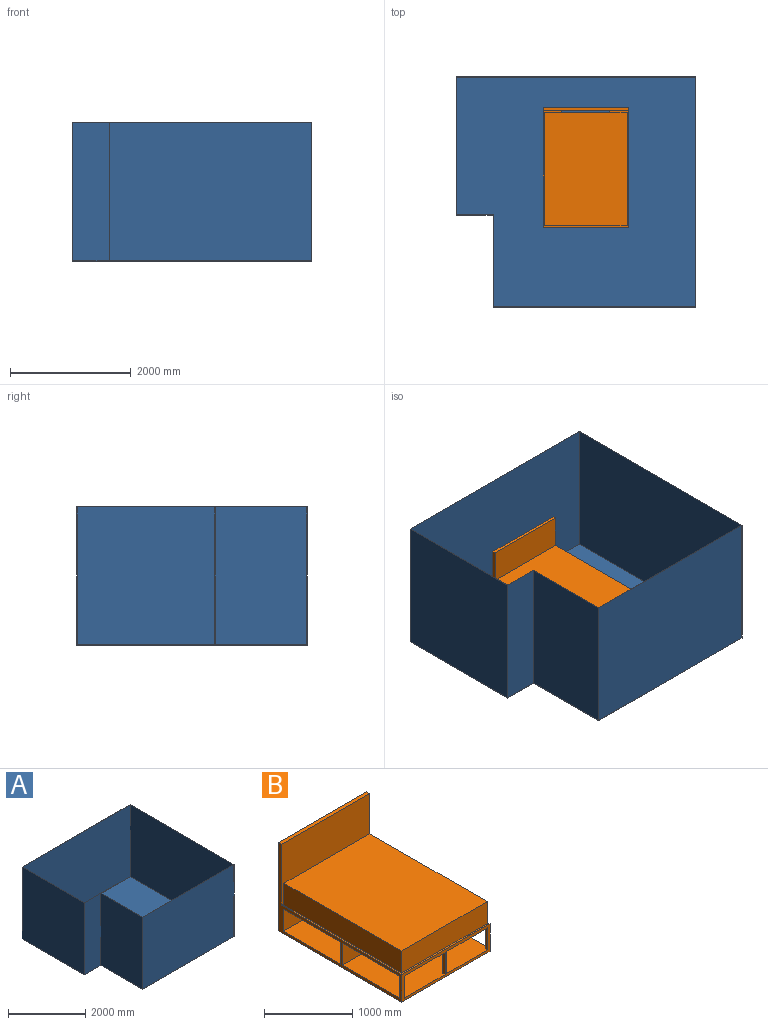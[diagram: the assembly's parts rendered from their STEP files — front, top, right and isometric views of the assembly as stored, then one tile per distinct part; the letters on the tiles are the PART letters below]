
ASSEMBLY  parts=2 mates=2
PART A: 15 faces, bbox 3962.4x3810x2286 mm
  f0: plane 3962.4x3810mm, normal (0,0,1), area 39458mm2, adj f1,f2,f3,f4,f5,f6,f8,f9
  f1: plane 3810x2286mm, normal (1,0,0), area 8709660mm2, adj f0,f2,f6,f7
  f2: plane 3962.4x2286mm, normal (0,1,0), area 9058046.4mm2, adj f0,f1,f3,f7
  f3: plane 2286x2286mm, normal (-1,0,0), area 5225796mm2, adj f0,f2,f4,f7
  f4: plane 2286x609.6mm, normal (0,-1,0), area 1393545.6mm2, adj f0,f3,f5,f7
  f5: plane 2286x1524mm, normal (-1,0,0), area 3483864mm2, adj f0,f4,f6,f7
  f6: plane 3352.8x2286mm, normal (0,-1,0), area 7664500.8mm2, adj f0,f1,f5,f7
  f7: plane 3962.4x3810mm, normal (0,0,-1), area 14167713.6mm2, adj f1,f2,f3,f4,f5,f6
  f8: plane 3804.92x2283.46mm, normal (-1,0,0), area 8688382.6mm2, adj f0,f9,f13,f14
  f9: plane 3957.32x2283.46mm, normal (0,-1,0), area 9036381.9mm2, adj f0,f8,f10,f14
  f10: plane 2283.46x2280.92mm, normal (1,0,0), area 5208389.6mm2, adj f0,f9,f11,f14
  f11: plane 2283.46x609.6mm, normal (0,1,0), area 1391997.2mm2, adj f0,f10,f12,f14
  f12: plane 2283.46x1524mm, normal (1,0,0), area 3479993mm2, adj f0,f11,f13,f14
  f13: plane 3347.72x2283.46mm, normal (0,1,0), area 7644384.7mm2, adj f0,f8,f12,f14
  f14: plane 3957.32x3804.92mm, normal (0,0,1), area 14128255.6mm2, adj f8,f9,f10,f11,f12,f13
PART B: 37 faces, bbox 1409.7x1981.2x1219.2 mm
  f0: plane 304.8x25.4mm, normal (0,1,0), area 7741.9mm2, adj f23,f24,f33,f36
  f1: plane 304.8x38.1mm, normal (0,1,0), area 11612.9mm2, adj f2,f23,f24,f35
  f2: plane 1981.2x1219.2mm, normal (-1,0,0), area 239999.5mm2, adj f1,f7,f8,f10,f11,f12,f13,f21
  f3: plane 1981.2x1219.2mm, normal (1,0,0), area 239999.5mm2, adj f7,f8,f10,f11,f12,f13,f20,f22
  f4: plane 1625.6x381mm, normal (-1,0,0), area 143225.5mm2, adj f5,f7,f9,f10,f11,f14,f22,f23
  f5: plane 800.1x38.1mm, normal (0,1,0), area 30483.8mm2, adj f4,f6,f10,f24
  f6: plane 1625.6x381mm, normal (1,0,0), area 143225.5mm2, adj f5,f7,f9,f10,f11,f14,f21,f23
  f7: plane 1930.4x1409.7mm, normal (0,0,1), area 122903mm2, adj f2,f3,f4,f6,f8,f11,f15,f16
  f8: plane 1409.7x381mm, normal (0,-1,0), area 138386.8mm2, adj f2,f3,f7,f10,f23,f24,f33,f34
  f9: plane 800.1x38.1mm, normal (0,1,0), area 30483.8mm2, adj f4,f6,f14,f23
  f10: plane 1981.2x1409.7mm, normal (0,0,-1), area 1492255.1mm2, adj f2,f3,f4,f5,f6,f8,f11,f12
  f11: plane 1409.7x1219.2mm, normal (0,-1,0), area 1486448.6mm2, adj f2,f3,f4,f6,f7,f10,f13
  f12: plane 1409.7x1219.2mm, normal (0,1,0), area 1718706.2mm2, adj f2,f3,f10,f13
  f13: plane 1409.7x50.8mm, normal (0,0,1), area 71612.8mm2, adj f2,f3,f11,f12
  f14: plane 1600.2x800.1mm, normal (0,0,-1), area 1280320mm2, adj f4,f6,f9,f15
  f15: plane 1371.6x304.8mm, normal (0,1,0), area 418063.7mm2, adj f7,f14,f16,f18,f19
  f16: plane 1879.6x304.8mm, normal (-1,0,0), area 572902.1mm2, adj f7,f15,f17,f19
  f17: plane 1371.6x304.8mm, normal (0,-1,0), area 418063.7mm2, adj f7,f16,f18,f19
  f18: plane 1879.6x304.8mm, normal (1,0,0), area 572902.1mm2, adj f7,f15,f17,f19
  f19: plane 1879.6x1371.6mm, normal (0,0,1), area 2578059.4mm2, adj f15,f16,f17,f18
  f20: plane 304.8x38.1mm, normal (0,1,0), area 11612.9mm2, adj f3,f23,f24,f34
  f21: plane 304.8x304.8mm, normal (0,-1,0), area 92903mm2, adj f2,f6,f23,f24
  f22: plane 304.8x304.8mm, normal (0,-1,0), area 92903mm2, adj f3,f4,f23,f24
  f23: plane 1409.7x952.5mm, normal (0,0,-1), area 820643.5mm2, adj f0,f1,f2,f3,f4,f6,f8,f9
  f24: plane 1409.7x952.5mm, normal (0,0,1), area 820643.5mm2, adj f0,f1,f2,f3,f4,f5,f6,f8
  f25: plane 304.8x304.8mm, normal (0,1,0), area 92903mm2, adj f2,f6,f26,f28
  f26: plane 914.4x304.8mm, normal (0,0,-1), area 278709.1mm2, adj f2,f6,f25,f27
  f27: plane 304.8x304.8mm, normal (0,-1,0), area 92903mm2, adj f2,f6,f26,f28
  f28: plane 914.4x304.8mm, normal (0,0,1), area 278709.1mm2, adj f2,f6,f25,f27
  f29: plane 914.4x304.8mm, normal (0,0,1), area 278709.1mm2, adj f3,f4,f30,f32
  f30: plane 304.8x304.8mm, normal (0,-1,0), area 92903mm2, adj f3,f4,f29,f31
  f31: plane 914.4x304.8mm, normal (0,0,-1), area 278709.1mm2, adj f3,f4,f30,f32
  f32: plane 304.8x304.8mm, normal (0,1,0), area 92903mm2, adj f3,f4,f29,f31
  f33: plane 304.8x38.1mm, normal (1,0,0), area 11612.9mm2, adj f0,f8,f23,f24
  f34: plane 304.8x38.1mm, normal (-1,0,0), area 11612.9mm2, adj f8,f20,f23,f24
  f35: plane 304.8x38.1mm, normal (1,0,0), area 11612.9mm2, adj f1,f8,f23,f24
  f36: plane 304.8x38.1mm, normal (-1,0,0), area 11612.9mm2, adj f0,f8,f23,f24
PLACE A t=(-2079.6,-3543.47,990.34)mm
PLACE B t=(-2224.78,-3821.5,1138.49)mm
MATE parallel B.f12 <-> A.f9  axis (0,1,0) through (-2224.78,-2145.1,1748.09)mm
MATE parallel B.f10 <-> A.f14  axis (0,0,-1) through (-2224.78,-3246.39,1138.49)mm
